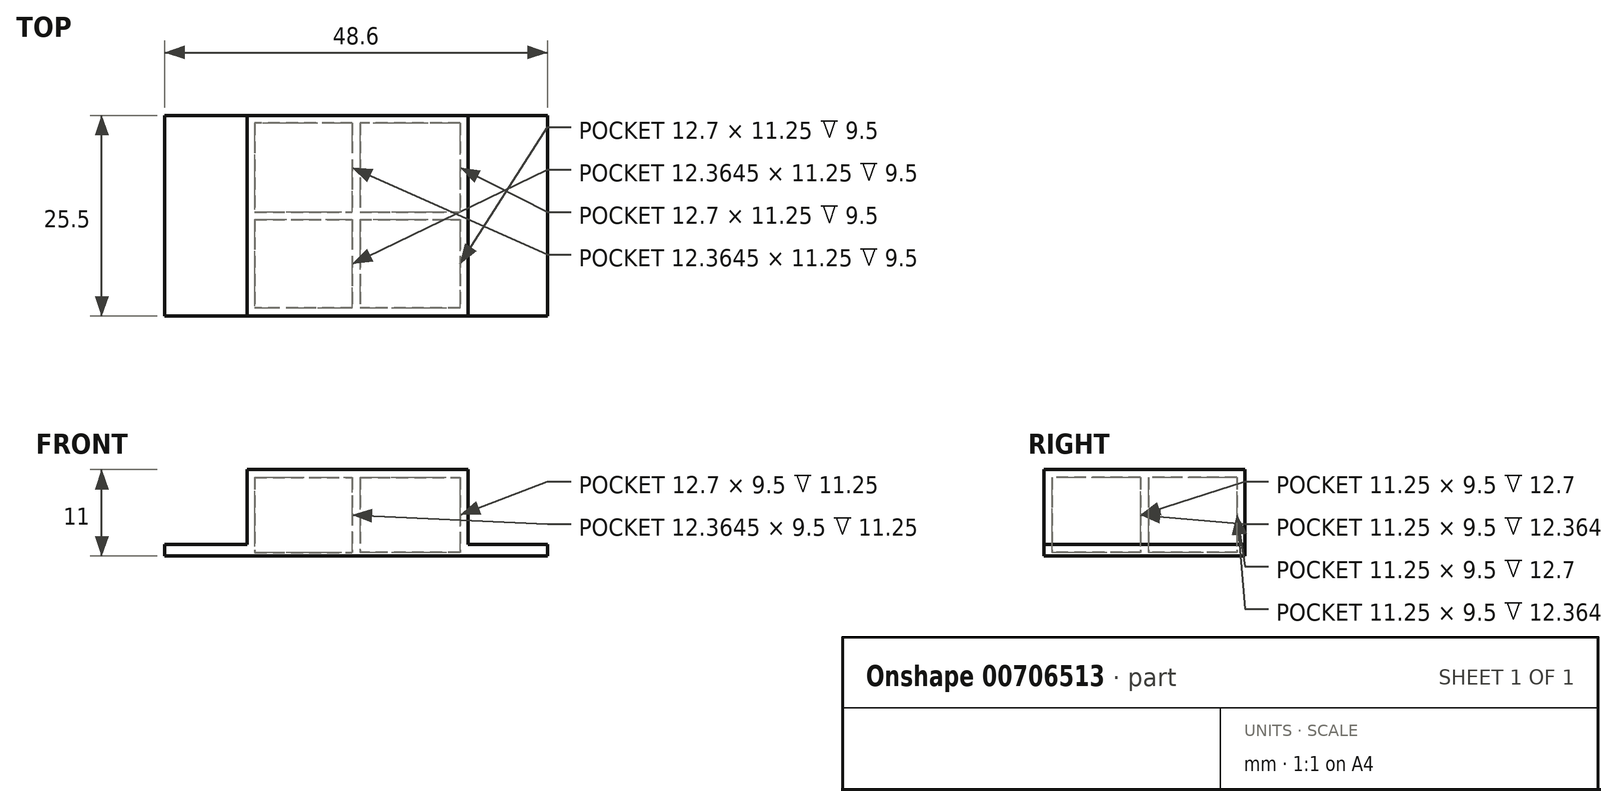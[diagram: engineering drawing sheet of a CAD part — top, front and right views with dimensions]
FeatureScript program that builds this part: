
annotation { "Feature Type Name" : "Feature", "Feature Type Description" : "" }
export const myFeature = defineFeature(function(context is Context, id is Id, definition is map)
    precondition{}
    {
        {
            var Q0;
            Q0=qCreatedBy(makeId("Top.planeOp"),FACE);
            var sketch = newSketch(context, id + "F0", { "sketchPlane" : qUnion([Q0])});
            skLineSegment(sketch, "E0.bottom", {"start": v(24.3, 12.75) * mm, "end": v(-24.3, 12.75) * mm});
            skLineSegment(sketch, "E0.top", {"start": v(24.3, -12.75) * mm, "end": v(-24.3, -12.75) * mm});
            skLineSegment(sketch, "E0.left", {"start": v(24.3, 12.75) * mm, "end": v(24.3, -12.75) * mm});
            skLineSegment(sketch, "E0.right", {"start": v(-24.3, 12.75) * mm, "end": v(-24.3, -12.75) * mm});
            skPoint(sketch, "E0.middle", {"position": v(0, 0) * mm});
            skLineSegment(sketch, "E1", {"start": v(-12.86, 11.75) * mm, "end": v(-12.86, 0.5) * mm});
            skLineSegment(sketch, "E2.0", {"start": v(23.3, 11.75) * mm, "end": v(23.3, -11.75) * mm});
            skLineSegment(sketch, "E2.1", {"start": v(23.3, 11.75) * mm, "end": v(14.2, 11.75) * mm});
            skLineSegment(sketch, "E2.2", {"start": v(-23.3, 11.75) * mm, "end": v(-23.3, -11.75) * mm});
            skLineSegment(sketch, "E2.3", {"start": v(23.3, -11.75) * mm, "end": v(14.2, -11.75) * mm});
            skLineSegment(sketch, "E3", {"start": v(14.2, 11.75) * mm, "end": v(14.2, -11.75) * mm});
            skLineSegment(sketch, "E4", {"start": v(13.2, 11.75) * mm, "end": v(13.2, 0.5) * mm});
            skLineSegment(sketch, "E5", {"start": v(-12.86, 0.5) * mm, "end": v(-0.5, 0.5) * mm});
            skLineSegment(sketch, "E6", {"start": v(-12.86, -0.5) * mm, "end": v(-0.5, -0.5) * mm});
            skLineSegment(sketch, "E7", {"start": v(-13.86, 12.75) * mm, "end": v(-13.86, -12.75) * mm});
            skLineSegment(sketch, "E8", {"start": v(-0.5, 11.75) * mm, "end": v(-0.5, 0.5) * mm});
            skLineSegment(sketch, "E9", {"start": v(0.5, 11.75) * mm, "end": v(0.5, 0.5) * mm});
            skLineSegment(sketch, "E10", {"start": v(14.2, -11.75) * mm, "end": v(14.2, -12.75) * mm});
            skLineSegment(sketch, "E11", {"start": v(13.7, -12.25) * mm, "end": v(-13.36, -12.25) * mm});
            skLineSegment(sketch, "E12", {"start": v(13.7, -12.25) * mm, "end": v(13.7, 12.25) * mm});
            skLineSegment(sketch, "E13", {"start": v(13.7, 12.25) * mm, "end": v(-13.36, 12.25) * mm});
            skLineSegment(sketch, "E14", {"start": v(-13.36, 12.25) * mm, "end": v(-13.36, -12.25) * mm});
            skPoint(sketch, "E15.orphan", {"position": v(-13.86, 12.25) * mm});
            skPoint(sketch, "E16.orphan", {"position": v(14.2, -12.25) * mm});
            skLineSegment(sketch, "E17.trimOffspring", {"start": v(13.2, -11.75) * mm, "end": v(0.5, -11.75) * mm});
            skPoint(sketch, "E18.trimOffspring.end.orphan", {"position": v(0, -12.75) * mm});
            skLineSegment(sketch, "E19.trimOffspring", {"start": v(-13.86, -11.75) * mm, "end": v(-23.3, -11.75) * mm});
            skPoint(sketch, "E20.orphan", {"position": v(0, 12.75) * mm});
            skLineSegment(sketch, "E21.trimOffspring", {"start": v(13.2, 11.75) * mm, "end": v(0.5, 11.75) * mm});
            skLineSegment(sketch, "E22", {"start": v(14.2, 11.75) * mm, "end": v(14.2, 12.75) * mm});
            skLineSegment(sketch, "E23.trimOffspring", {"start": v(-12.86, -0.5) * mm, "end": v(-12.86, -11.75) * mm});
            skLineSegment(sketch, "E24.trimOffspring", {"start": v(-0.5, -0.5) * mm, "end": v(-0.5, -11.75) * mm});
            skLineSegment(sketch, "E25.trimOffspring", {"start": v(0.5, 0.5) * mm, "end": v(13.2, 0.5) * mm});
            skLineSegment(sketch, "E26.trimOffspring", {"start": v(0.5, -0.5) * mm, "end": v(0.5, -11.75) * mm});
            skLineSegment(sketch, "E27.trimOffspring", {"start": v(0.5, -0.5) * mm, "end": v(13.2, -0.5) * mm});
            skLineSegment(sketch, "E28.trimOffspring", {"start": v(13.2, -0.5) * mm, "end": v(13.2, -11.75) * mm});
            skLineSegment(sketch, "E29.trimOffspring", {"start": v(-0.5, 11.75) * mm, "end": v(-12.86, 11.75) * mm});
            skLineSegment(sketch, "E30.trimOffspring", {"start": v(-13.86, 11.75) * mm, "end": v(-23.3, 11.75) * mm});
            skLineSegment(sketch, "E31.trimOffspring", {"start": v(-0.5, -11.75) * mm, "end": v(-12.86, -11.75) * mm});
            skSolve(sketch);
        }
        {
            var Q0;
            Q0=makeQuery(id+"F0.imprint","IMPRINT",FACE,{"disambiguationData":[TD([[makeQuery(id+"F0.imprint","IMPRINT",EDGE,{"derivedFrom":sQuery(id+"F0.wireOp",EDGE,"E2.0")}),-1.0]])]});
            var Q1;
            {var subQ0=sQuery(id+"F0.wireOp",EDGE,"E0.left");Q1=makeQuery(id+"F0.imprint","IMPRINT",FACE,{"disambiguationData":[TD([[makeQuery(id+"F0.imprint","IMPRINT",EDGE,{"derivedFrom":subQ0}),-1.0]])]});}
            var Q2;
            {var subQ1=sQuery(id+"F0.wireOp",EDGE,"E0.right");Q2=makeQuery(id+"F0.imprint","IMPRINT",FACE,{"disambiguationData":[TD([[makeQuery(id+"F0.imprint","IMPRINT",EDGE,{"derivedFrom":subQ1}),1.0]])]});}
            var Q3;
            {var subQ0=sQuery(id+"F0.wireOp",EDGE,"E2.2");Q3=makeQuery(id+"F0.imprint","IMPRINT",FACE,{"disambiguationData":[TD([[makeQuery(id+"F0.imprint","IMPRINT",EDGE,{"derivedFrom":subQ0}),1.0]])]});}
            extrude(context, id + "F1", {"entities" : qUnion([Q0, Q1, Q2, Q3]), "depth" : 1.5 * mm, "offsetDistance" : 25 * mm});
        }
        {
            var Q0;
            {var subQ0=sQuery(id+"F0.wireOp",EDGE,"E5");var subQ1=sQuery(id+"F0.wireOp",EDGE,"E1");var subQ2=makeQuery(id+"F0.imprint","INTERSECT",VERTEX,{"derivedFrom":[subQ1,subQ0]});Q0=makeQuery(id+"F0.imprint","IMPRINT",FACE,{"disambiguationData":[TD([[makeQuery(id+"F0.imprint","IMPRINT",EDGE,{"disambiguationData":[TD([[subQ2,1.0]])],"derivedFrom":subQ1}),1.0]])]});}
            var Q1;
            {var subQ0=sQuery(id+"F0.wireOp",EDGE,"E21.trimOffspring");var subQ1=sQuery(id+"F0.wireOp",EDGE,"E4");var subQ2=makeQuery(id+"F0.imprint","INTERSECT",VERTEX,{"derivedFrom":[subQ1,subQ0]});Q1=makeQuery(id+"F0.imprint","IMPRINT",FACE,{"disambiguationData":[TD([[makeQuery(id+"F0.imprint","IMPRINT",EDGE,{"disambiguationData":[TD([[subQ2,-1.0]])],"derivedFrom":subQ1}),-1.0]])]});}
            var Q2;
            {var subQ0=sQuery(id+"F0.wireOp",EDGE,"E17.trimOffspring");var subQ1=sQuery(id+"F0.wireOp",EDGE,"E4");var subQ2=makeQuery(id+"F0.imprint","INTERSECT",VERTEX,{"derivedFrom":[subQ1,subQ0]});Q2=makeQuery(id+"F0.imprint","IMPRINT",FACE,{"disambiguationData":[TD([[makeQuery(id+"F0.imprint","IMPRINT",EDGE,{"disambiguationData":[TD([[subQ2,1.0]])],"derivedFrom":subQ1}),-1.0]])]});}
            var Q3;
            {var subQ0=sQuery(id+"F0.wireOp",EDGE,"E17.trimOffspring");var subQ1=sQuery(id+"F0.wireOp",EDGE,"E1");var subQ2=makeQuery(id+"F0.imprint","INTERSECT",VERTEX,{"derivedFrom":[subQ1,subQ0]});Q3=makeQuery(id+"F0.imprint","IMPRINT",FACE,{"disambiguationData":[TD([[makeQuery(id+"F0.imprint","IMPRINT",EDGE,{"disambiguationData":[TD([[subQ2,1.0]])],"derivedFrom":subQ1}),1.0]])]});}
            var Q4;
            Q4=makeQuery(id+"F0.imprint","IMPRINT",FACE,{"disambiguationData":[TD([[makeQuery(id+"F0.imprint","IMPRINT",EDGE,{"derivedFrom":sQuery(id+"F0.wireOp",EDGE,"E6")}),-1.0]])]});
            var Q5;
            Q5=makeQuery(id+"F0.imprint","IMPRINT",FACE,{"disambiguationData":[TD([[makeQuery(id+"F0.imprint","IMPRINT",EDGE,{"derivedFrom":sQuery(id+"F0.wireOp",EDGE,"E17.trimOffspring")}),-1.0]])]});
            extrude(context, id + "F2", {"entities" : qUnion([Q0, Q1, Q2, Q3, Q4, Q5]), "operationType" : NewBodyOperationType.ADD, "depth" : .5 * mm, "offsetDistance" : 25 * mm});
        }
        {
            var Q0;
            Q0=makeQuery(id+"F0.imprint","IMPRINT",FACE,{"disambiguationData":[TD([[makeQuery(id+"F0.imprint","IMPRINT",EDGE,{"derivedFrom":sQuery(id+"F0.wireOp",EDGE,"E3")}),-1.0]])]});
            extrude(context, id + "F3", {"entities" : qUnion([Q0]), "operationType" : NewBodyOperationType.ADD, "depth" : 6 * mm, "offsetDistance" : 25 * mm});
        }
        {
            var Q0;
            Q0=makeQuery(id+"F0.imprint","IMPRINT",FACE,{"disambiguationData":[TD([[makeQuery(id+"F0.imprint","IMPRINT",EDGE,{"derivedFrom":sQuery(id+"F0.wireOp",EDGE,"E1")}),-1.0]])]});
            extrude(context, id + "F4", {"entities" : qUnion([Q0]), "operationType" : NewBodyOperationType.ADD, "depth" : 10 * mm, "offsetDistance" : 25 * mm});
        }
        {
            var Q0;
            Q0=makeQuery(id+"F3.opExtrude","CAP_FACE",FACE,{"disambiguationData":[OSD([sQuery(id+"F0.wireOp",EDGE,"E0.bottom"),sQuery(id+"F0.wireOp",EDGE,"E0.top"),sQuery(id+"F0.wireOp",EDGE,"E3"),sQuery(id+"F0.wireOp",EDGE,"E7"),sQuery(id+"F0.wireOp",EDGE,"E10"),sQuery(id+"F0.wireOp",EDGE,"E11"),sQuery(id+"F0.wireOp",EDGE,"E12"),sQuery(id+"F0.wireOp",EDGE,"E13"),sQuery(id+"F0.wireOp",EDGE,"E14"),sQuery(id+"F0.wireOp",EDGE,"E22")])],"isStart":false});
            var sketch = newSketch(context, id + "F5", { "sketchPlane" : qUnion([Q0])});
            skLineSegment(sketch, "E32.bottom", {"start": v(-13.36, 12.25) * mm, "end": v(13.7, 12.25) * mm});
            skLineSegment(sketch, "E32.top", {"start": v(-13.36, -12.25) * mm, "end": v(13.7, -12.25) * mm});
            skLineSegment(sketch, "E32.left", {"start": v(-13.36, 12.25) * mm, "end": v(-13.36, -12.25) * mm});
            skLineSegment(sketch, "E32.right", {"start": v(13.7, 12.25) * mm, "end": v(13.7, -12.25) * mm});
            skLineSegment(sketch, "E33.bottom", {"start": v(-13.86, 12.75) * mm, "end": v(14.2, 12.75) * mm});
            skLineSegment(sketch, "E33.top", {"start": v(-13.86, -12.75) * mm, "end": v(14.2, -12.75) * mm});
            skLineSegment(sketch, "E33.left", {"start": v(-13.86, 12.75) * mm, "end": v(-13.86, -12.75) * mm});
            skLineSegment(sketch, "E33.right", {"start": v(14.2, 12.75) * mm, "end": v(14.2, -12.75) * mm});
            skSolve(sketch);
        }
        {
            var Q0;
            Q0 = qSketchRegion(id + "F5", true);
            extrude(context, id + "F6", {"entities" : qUnion([Q0]), "depth" : 4 * mm, "offsetDistance" : 25 * mm});
        }
        {
            var Q0;
            Q0=makeQuery(id+"F6.opExtrude","CAP_FACE",FACE,{"disambiguationData":[OSD([sQuery(id+"F5.wireOp",EDGE,"E32.bottom"),sQuery(id+"F5.wireOp",EDGE,"E32.top"),sQuery(id+"F5.wireOp",EDGE,"E32.left"),sQuery(id+"F5.wireOp",EDGE,"E32.right"),sQuery(id+"F5.wireOp",EDGE,"E33.bottom"),sQuery(id+"F5.wireOp",EDGE,"E33.top"),sQuery(id+"F5.wireOp",EDGE,"E33.left"),sQuery(id+"F5.wireOp",EDGE,"E33.right")])],"isStart":false});
            var sketch = newSketch(context, id + "F7", { "sketchPlane" : qUnion([Q0])});
            skLineSegment(sketch, "E34.bottom", {"start": v(-13.86, 12.75) * mm, "end": v(14.2, 12.75) * mm});
            skLineSegment(sketch, "E34.top", {"start": v(-13.86, -12.75) * mm, "end": v(14.2, -12.75) * mm});
            skLineSegment(sketch, "E34.left", {"start": v(-13.86, 12.75) * mm, "end": v(-13.86, -12.75) * mm});
            skLineSegment(sketch, "E34.right", {"start": v(14.2, 12.75) * mm, "end": v(14.2, -12.75) * mm});
            skSolve(sketch);
        }
        {
            var Q0;
            Q0 = qSketchRegion(id + "F7", true);
            extrude(context, id + "F8", {"entities" : qUnion([Q0]), "operationType" : NewBodyOperationType.ADD, "depth" : 1 * mm, "offsetDistance" : 25 * mm});
        }
    });
